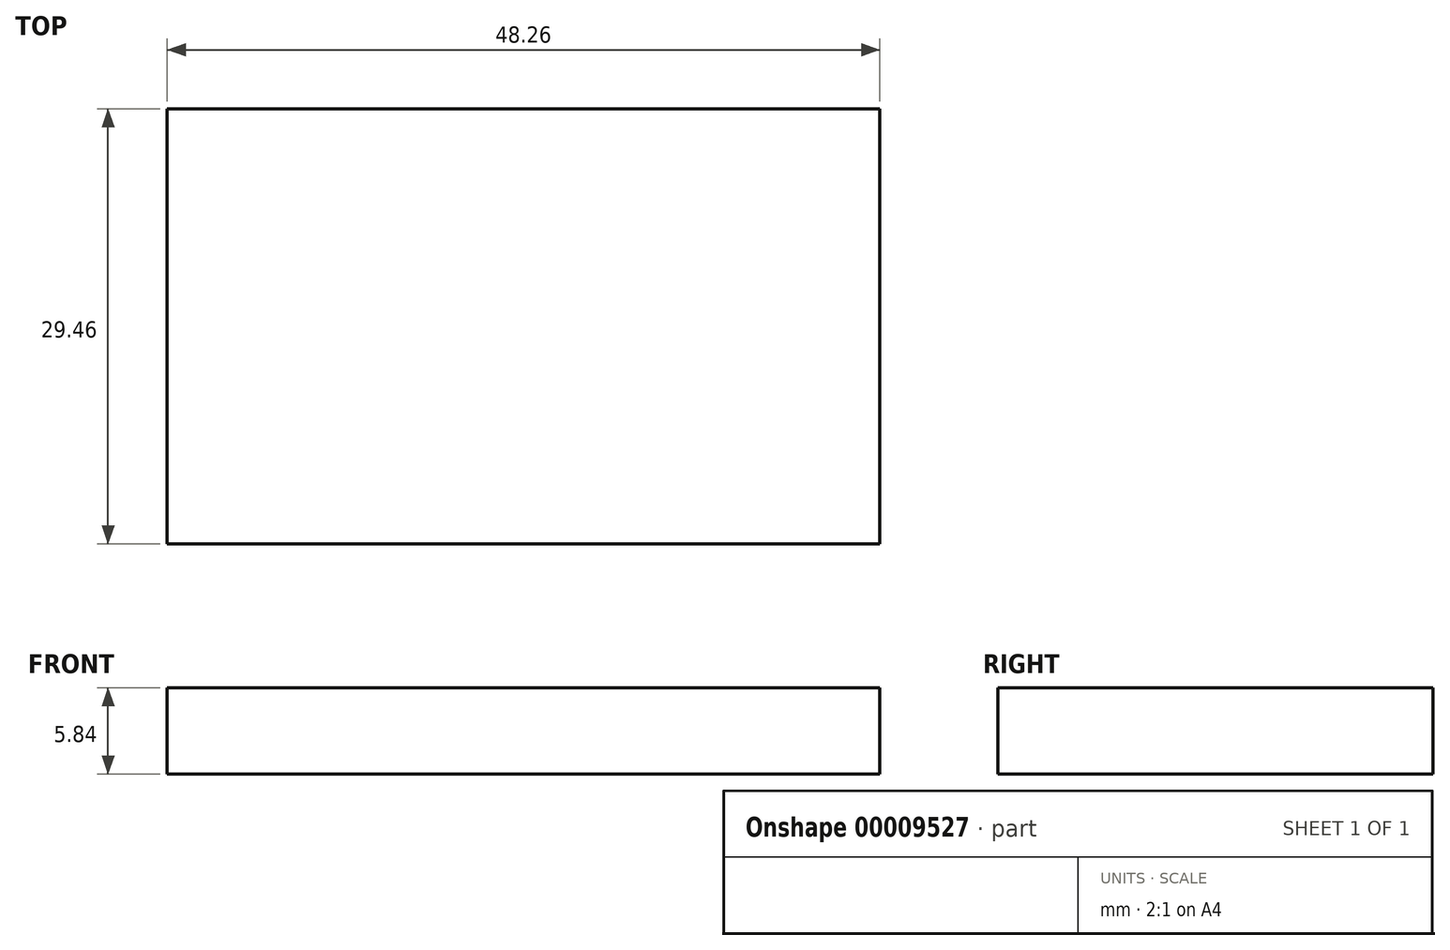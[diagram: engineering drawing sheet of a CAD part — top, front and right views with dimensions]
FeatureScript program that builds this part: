
annotation { "Feature Type Name" : "Feature", "Feature Type Description" : "" }
export const myFeature = defineFeature(function(context is Context, id is Id, definition is map)
    precondition{}
    {
        {
            var Q0;
            Q0=qCreatedBy(makeId("Top.planeOp"),FACE);
            var sketch = newSketch(context, id + "F0", { "sketchPlane" : qUnion([Q0])});
            skLineSegment(sketch, "E0.bottom", {"start": v(0, 0) * mm, "end": v(48.26, 0) * mm});
            skLineSegment(sketch, "E0.top", {"start": v(0, -29.46) * mm, "end": v(48.26, -29.46) * mm});
            skLineSegment(sketch, "E0.left", {"start": v(0, 0) * mm, "end": v(0, -29.46) * mm});
            skLineSegment(sketch, "E0.right", {"start": v(48.26, 0) * mm, "end": v(48.26, -29.46) * mm});
            skSolve(sketch);
        }
        {
            var Q0;
            Q0=makeQuery(id+"F0.imprint","IMPRINT",FACE,{"disambiguationData":[TD([[makeQuery(id+"F0.imprint","IMPRINT",EDGE,{"derivedFrom":sQuery(id+"F0.wireOp",EDGE,"E0.bottom")}),-1.0]])]});
            extrude(context, id + "F1", {"entities" : qUnion([Q0]), "depth" : 5.84 * mm});
        }
    });
